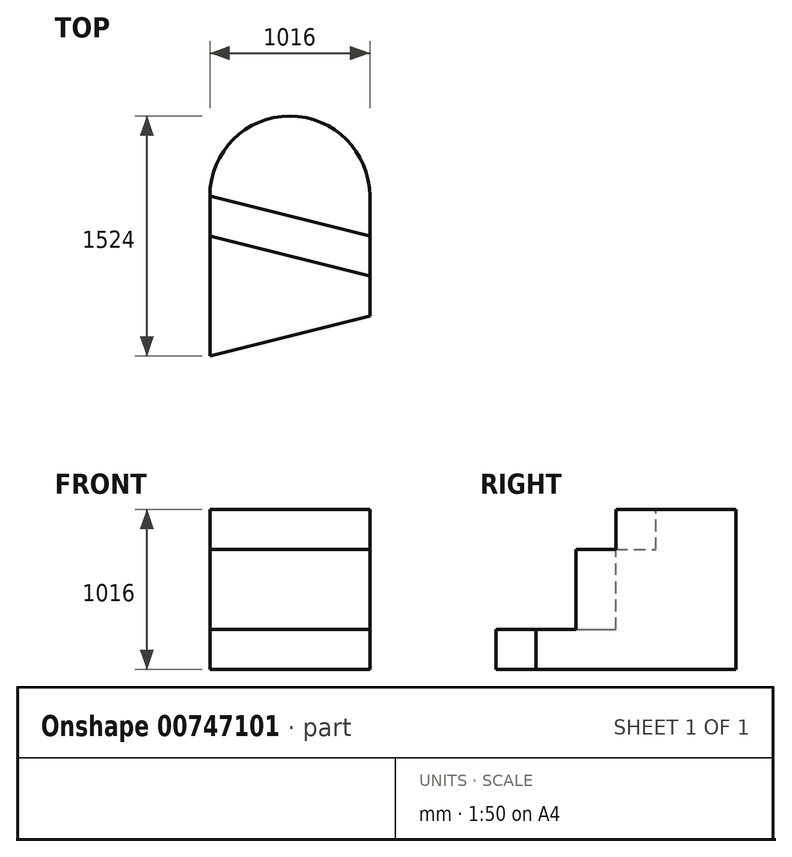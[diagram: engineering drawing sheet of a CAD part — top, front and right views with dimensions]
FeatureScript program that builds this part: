
annotation { "Feature Type Name" : "Feature", "Feature Type Description" : "" }
export const myFeature = defineFeature(function(context is Context, id is Id, definition is map)
    precondition{}
    {
        {
            var Q0;
            Q0=qCreatedBy(makeId("Front.planeOp"),FACE);
            var sketch = newSketch(context, id + "F0", { "sketchPlane" : qUnion([Q0])});
            skLineSegment(sketch, "E0.bottom", {"start": v(-526.19, 630.42) * mm, "end": v(489.81, 630.42) * mm});
            skLineSegment(sketch, "E0.top", {"start": v(-526.19, -385.58) * mm, "end": v(489.81, -385.58) * mm});
            skLineSegment(sketch, "E0.left", {"start": v(-526.19, 630.42) * mm, "end": v(-526.19, -385.58) * mm});
            skLineSegment(sketch, "E0.right", {"start": v(489.81, 630.42) * mm, "end": v(489.81, -385.58) * mm});
            skSolve(sketch);
        }
        {
            var Q0;
            Q0 = qSketchRegion(id + "F0", true);
            extrude(context, id + "F1", {"entities" : qUnion([Q0]), "depth" : 1524 * mm, "offsetDistance" : 25.4 * mm});
        }
        {
            var Q0;
            Q0=makeQuery(id+"F1.opExtrude","SWEPT_FACE",FACE,{"disambiguationData":[OSD([sQuery(id+"F0.wireOp",EDGE,"E0.bottom")])]});
            var sketch = newSketch(context, id + "F2", { "sketchPlane" : qUnion([Q0])});
            skLineSegment(sketch, "E1", {"start": v(-526.19, 0) * mm, "end": v(-526.19, -508) * mm});
            skLineSegment(sketch, "E2", {"start": v(-526.19, 0) * mm, "end": v(-18.19, 0) * mm});
            skLineSegment(sketch, "E3", {"start": v(-18.19, 0) * mm, "end": v(-18.19, -508) * mm});
            skCircle(sketch, "E4", {"center": v(-18.19, -508) * mm, "radius": 508 * mm});
            skSolve(sketch);
        }
        {
            var Q0;
            {var subQ0=sQuery(id+"F2.wireOp",EDGE,"E1");Q0=makeQuery(id+"F2.imprint","IMPRINT",FACE,{"disambiguationData":[TD([[makeQuery(id+"F2.imprint","IMPRINT",EDGE,{"derivedFrom":subQ0}),-1.0]])]});}
            var Q1;
            {var subQ0=sQuery(id+"F2.wireOp",EDGE,"E4");var subQ1=sQuery(id+"F0.wireOp",EDGE,"E0.bottom");var subQ2=makeQuery(id+"F1.opExtrude","CAP_EDGE",EDGE,{"disambiguationData":[OSD([subQ1])],"isStart":true});var subQ3=makeQuery(id+"F2.imprint","INTERSECT",VERTEX,{"derivedFrom":[subQ2,sQuery(id+"F2.wireOp",EDGE,"E2"),subQ0]});Q1=makeQuery(id+"F2.imprint","IMPRINT",FACE,{"disambiguationData":[TD([[makeQuery(id+"F2.imprint","IMPRINT",EDGE,{"disambiguationData":[TD([[subQ3,1.0]])],"derivedFrom":subQ0}),-1.0]])]});}
            extrude(context, id + "F3", {"entities" : qUnion([Q0, Q1]), "operationType" : NewBodyOperationType.REMOVE, "oppositeDirection" : true, "depth" : 1016 * mm, "offsetDistance" : 25.4 * mm});
        }
        {
            var Q0;
            Q0=makeQuery(id+"F1.opExtrude","SWEPT_FACE",FACE,{"disambiguationData":[OSD([sQuery(id+"F0.wireOp",EDGE,"E0.bottom")])]});
            var sketch = newSketch(context, id + "F4", { "sketchPlane" : qUnion([Q0])});
            skPoint(sketch, "E5", {"position": v(-526.19, -508) * mm});
            skPoint(sketch, "E6", {"position": v(489.81, -508) * mm});
            skLineSegment(sketch, "E7", {"start": v(489.81, -508) * mm, "end": v(489.81, -762) * mm});
            skLineSegment(sketch, "E8", {"start": v(-526.19, -508) * mm, "end": v(489.81, -762) * mm});
            skLineSegment(sketch, "E9", {"start": v(489.81, -762) * mm, "end": v(489.81, -1016) * mm});
            skLineSegment(sketch, "E10", {"start": v(489.81, -1016) * mm, "end": v(-526.19, -762) * mm});
            skLineSegment(sketch, "E11", {"start": v(-526.19, -762) * mm, "end": v(-526.19, -508) * mm});
            skSolve(sketch);
        }
        {
            var Q0;
            Q0=makeQuery(id+"F4.imprint","IMPRINT",FACE,{"disambiguationData":[TD([[makeQuery(id+"F4.imprint","IMPRINT",EDGE,{"derivedFrom":sQuery(id+"F4.wireOp",EDGE,"E8")}),-1.0]])]});
            extrude(context, id + "F5", {"entities" : qUnion([Q0]), "operationType" : NewBodyOperationType.REMOVE, "oppositeDirection" : true, "depth" : 254 * mm, "offsetDistance" : 25.4 * mm});
        }
        {
            var Q0;
            {var subQ1=sQuery(id+"F0.wireOp",EDGE,"E0.left");var subQ2=sQuery(id+"F0.wireOp",EDGE,"E0.bottom");Q0=makeQuery(id+"F5.boolean.opBoolean","SPLIT",FACE,{"disambiguationData":[TD([makeQuery(id+"F1.opExtrude","SWEPT_FACE",FACE,{"disambiguationData":[OSD([subQ1])]})])],"derivedFrom":makeQuery(id+"F1.opExtrude","SWEPT_FACE",FACE,{"disambiguationData":[OSD([subQ2])]})});}
            var sketch = newSketch(context, id + "F6", { "sketchPlane" : qUnion([Q0])});
            skLineSegment(sketch, "E12", {"start": v(489.81, -1016) * mm, "end": v(489.81, -1270) * mm});
            skLineSegment(sketch, "E13", {"start": v(489.81, -1270) * mm, "end": v(-526.19, -1524) * mm});
            skSolve(sketch);
        }
        {
            var Q0;
            Q0 = qSketchRegion(id + "F6", true);
            var Q1;
            {var subQ0=sQuery(id+"F6.wireOp",EDGE,"E13");Q1=makeQuery(id+"F6.imprint","IMPRINT",FACE,{"disambiguationData":[TD([[makeQuery(id+"F6.imprint","IMPRINT",EDGE,{"derivedFrom":subQ0}),1.0]])]});}
            extrude(context, id + "F7", {"entities" : qUnion([Q0, Q1]), "operationType" : NewBodyOperationType.REMOVE, "oppositeDirection" : true, "depth" : 1016 * mm, "offsetDistance" : 25.4 * mm});
        }
        {
            var Q0;
            {var subQ1=sQuery(id+"F0.wireOp",EDGE,"E0.left");var subQ2=sQuery(id+"F0.wireOp",EDGE,"E0.bottom");Q0=makeQuery(id+"F5.boolean.opBoolean","SPLIT",FACE,{"disambiguationData":[TD([makeQuery(id+"F1.opExtrude","SWEPT_FACE",FACE,{"disambiguationData":[OSD([subQ1])]})])],"derivedFrom":makeQuery(id+"F1.opExtrude","SWEPT_FACE",FACE,{"disambiguationData":[OSD([subQ2])]})});}
            extrude(context, id + "F8", {"entities" : qUnion([Q0]), "operationType" : NewBodyOperationType.REMOVE, "oppositeDirection" : true, "depth" : 762 * mm, "offsetDistance" : 25.4 * mm});
        }
    });
